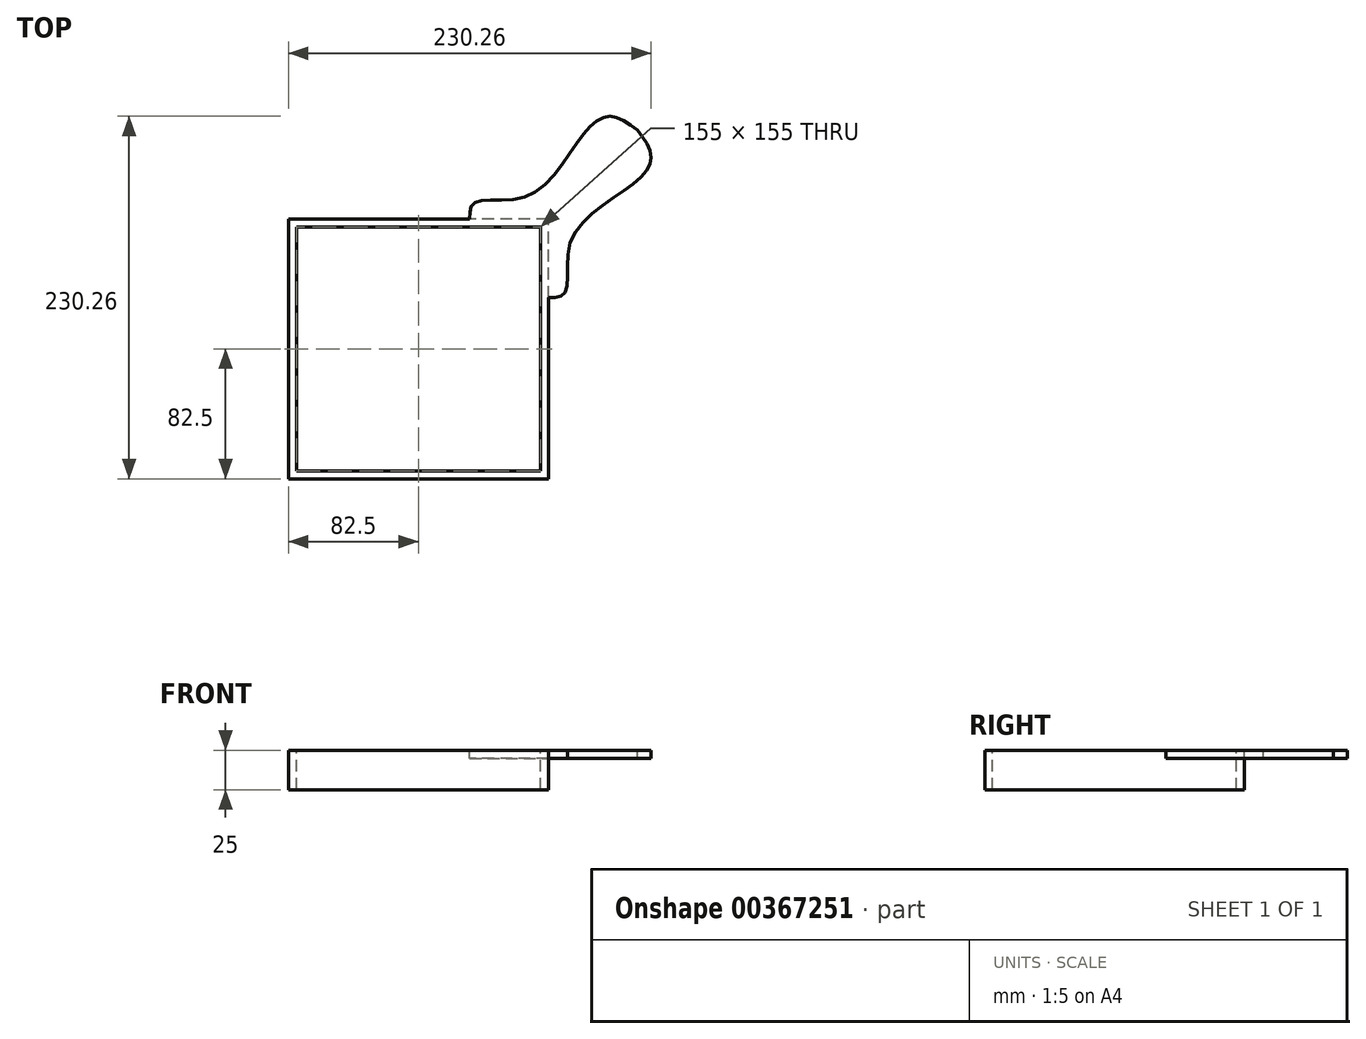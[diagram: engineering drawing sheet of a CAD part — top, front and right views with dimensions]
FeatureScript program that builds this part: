
annotation { "Feature Type Name" : "Feature", "Feature Type Description" : "" }
export const myFeature = defineFeature(function(context is Context, id is Id, definition is map)
    precondition{}
    {
        {
            var Q0;
            Q0=qCreatedBy(makeId("Top.planeOp"),FACE);
            var sketch = newSketch(context, id + "F0", { "sketchPlane" : qUnion([Q0])});
            skLineSegment(sketch, "E0.bottom", {"start": v(82.5, -82.5) * mm, "end": v(-82.5, -82.5) * mm});
            skLineSegment(sketch, "E0.top", {"start": v(82.5, 82.5) * mm, "end": v(-82.5, 82.5) * mm});
            skLineSegment(sketch, "E0.left", {"start": v(82.5, -82.5) * mm, "end": v(82.5, 82.5) * mm});
            skLineSegment(sketch, "E0.right", {"start": v(-82.5, -82.5) * mm, "end": v(-82.5, 82.5) * mm});
            skPoint(sketch, "E0.middle", {"position": v(0, 0) * mm});
            skLineSegment(sketch, "E1.bottom", {"start": v(77.5, -77.5) * mm, "end": v(-77.5, -77.5) * mm});
            skLineSegment(sketch, "E1.top", {"start": v(77.5, 77.5) * mm, "end": v(-77.5, 77.5) * mm});
            skLineSegment(sketch, "E1.left", {"start": v(77.5, -77.5) * mm, "end": v(77.5, 77.5) * mm});
            skLineSegment(sketch, "E1.right", {"start": v(-77.5, -77.5) * mm, "end": v(-77.5, 77.5) * mm});
            skLineSegment(sketch, "E2", {"start": v(82.5, 82.5) * mm, "end": v(32.5, 82.5) * mm, "construction": true});
            skLineSegment(sketch, "E3", {"start": v(82.5, 82.5) * mm, "end": v(82.5, 32.5) * mm, "construction": true});
            skLineSegment(sketch, "E4", {"start": v(0, 0) * mm, "end": v(82.5, 82.5) * mm, "construction": true});
            skLineSegment(sketch, "E5", {"start": v(82.5, 82.5) * mm, "end": v(139.07, 139.07) * mm, "construction": true});
            skFitSpline(sketch, "E6", {"points": [v(32.5, 82.5) * mm, v(35.88, 93.1) * mm, v(69.38, 97.15) * mm, v(103.84, 135.17) * mm, v(121.66, 147.76) * mm, v(139.07, 139.07) * mm], "startDerivative": vector(1.07, 99.46) * mm, "endDerivative": vector(101.44, -74.54) * mm});
            skFitSpline(sketch, "E7.MirrorCS", {"points": [v(82.5, 32.5) * mm, v(93.1, 35.88) * mm, v(97.15, 69.38) * mm, v(135.17, 103.84) * mm, v(147.76, 121.66) * mm, v(139.07, 139.07) * mm], "startDerivative": vector(99.46, 1.07) * mm, "endDerivative": vector(-74.54, 101.44) * mm});
            skSolve(sketch);
        }
        {
            var Q0;
            {var subQ1=sQuery(id+"F0.wireOp",EDGE,"E0.bottom");Q0=makeQuery(id+"F0.imprint","IMPRINT",FACE,{"disambiguationData":[TD([[makeQuery(id+"F0.imprint","IMPRINT",EDGE,{"derivedFrom":subQ1}),-1.0]])]});}
            extrude(context, id + "F1", {"entities" : qUnion([Q0]), "oppositeDirection" : true, "depth" : 25 * mm});
        }
        {
            var Q0;
            {var subQ3=sQuery(id+"F0.wireOp",EDGE,"E6");Q0=makeQuery(id+"F0.imprint","IMPRINT",FACE,{"disambiguationData":[TD([[makeQuery(id+"F0.imprint","IMPRINT",EDGE,{"derivedFrom":subQ3}),-1.0]])]});}
            extrude(context, id + "F2", {"entities" : qUnion([Q0]), "operationType" : NewBodyOperationType.ADD, "oppositeDirection" : true, "depth" : 5 * mm});
        }
    });
